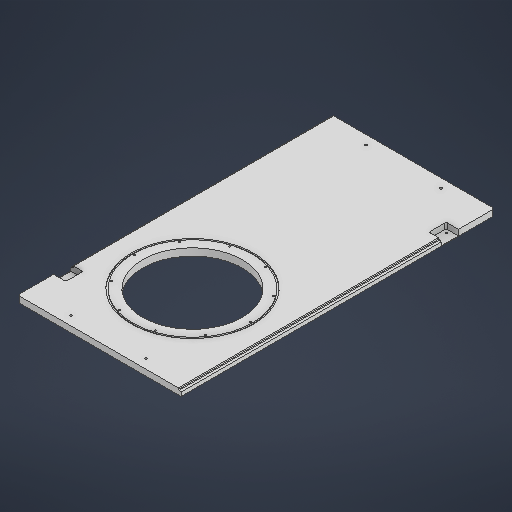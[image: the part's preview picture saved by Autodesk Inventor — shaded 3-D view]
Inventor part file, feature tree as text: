
AUTODESK INVENTOR PART (.ipt)
format: ipt  version: 2025 (Build 290162000, 162)  size: 413,184 bytes
history: native  units: in
note: dims shown in document units (in); Inventor stores cm internally (conversion verified against a paired STEP export)
features: sketch x9, extrude x5, chamfer x5, hole x3, plane x1, fillet x1
ambient origin geometry x8: Origin, YZ Plane, XZ Plane, XY Plane, X Axis, Y Axis, Z Axis, Center Point
bodies: Solid1 (feature_tree)
feature tree (24):
  extrude  "Extrusion1"  Depth=27.1654in
  sketch  "Sketch2"  dims[d2=0.625in d3=0.0in d4=8.0709in]
  extrude  "Extrusion2"  Depth=0.625in
  plane  "Work Plane1"
  hole  "Hole3"  [1 undecoded]
  extrude  "Extrusion6"  Depth=5.9055in
  hole  "Hole4"  [1 undecoded]
  sketch  "Sketch9"  dims[d65=10.6299in d66=0.0984in d67=0.0in]
  fillet  "Fillet2"  Radius=10.3543in
  chamfer  "Chamfer1"  Distance=0.0984in
  chamfer  "Chamfer2"  Distance=3.937in Angle=360.0deg
  extrude  "Extrusion7"  Depth=1.063in
  extrude  "Extrusion8"  Depth=1.063in
  chamfer  "Chamfer3"  Distance=1.4961in
  chamfer  "Chamfer4"  Distance=1.4961in
  hole  "Hole5"  [1 undecoded]
  chamfer  "Chamfer5"  Distance=3.1102in
  sketch  "Sketch1"  dims[d0=14.1732in d1=27.1654in]
  sketch  "Sketch6"  dims[d8=10.6299in d50=5.9055in]
  sketch  "Sketch7"  dims[d55=6.5in d56=25.5906in]
  sketch  "Sketch8"  dims[d57=0.1936in d58=0.1969in d59=0.1575in d60=0.0787in d61=90.0deg d62=0.1969in d63=0.8108in d64=10.3543in]
  sketch  "Sketch Circular Pattern4"  dims[d5=8.6614in d6=0.0in d7=0.0in]
  sketch  "Sketch10"  dims[d68=10.0394in]
  sketch  "Sketch11"  dims[d69=0.1575in d70=3.937in d72=360.0deg d74=0.1628in d75=0.3937in d76=0.1575in d77=0.0787in d78=90.0deg d79=0.3937in d80=0.8108in d82=1.063in d83=1.063in d84=1.4961in d85=1.4961in d86=3.1102in d87=3.1102in d88=0.1969in d89=0.0984in d90=0.0787in d91=45.0deg d92=0.0984in d93=0.0787in d94=45.0deg d95=0.1181in d96=0.1181in d97=0.4951in d98=0.0in d99=0.2362in d100=0.2362in d101=0.122in d102=0.0in d103=0.0787in d104=0.1378in d105=45.0deg d106=0.1378in d107=0.0787in d108=45.0deg d109=0.748in d110=0.315in d111=0.8661in d112=0.748in d113=0.1299in d114=0.1299in d115=0.1299in d116=0.1299in d118=0.315in d119=0.8661in d120=0.748in d121=0.748in d122=0.1276in d123=0.315in d124=0.1575in d125=0.0787in d126=90.0deg d127=0.315in d128=0.8108in d129=0.0138in d130=0.0787in d131=45.0deg d26=0.0394in d27=0.0394in d28=0.0394in d29=0.0059in d30=0.0098in d31=0.0148in d32=0.5635in d33=0.0295in d34=0.8108in d35=0.0025in d36=0.0295in d37=0.0148in]
note: 3 required parameter values undecoded (feature->parameter linkage not recoverable at this tier; creation-order binding heuristic only, values carry confidence <= 0.55)
